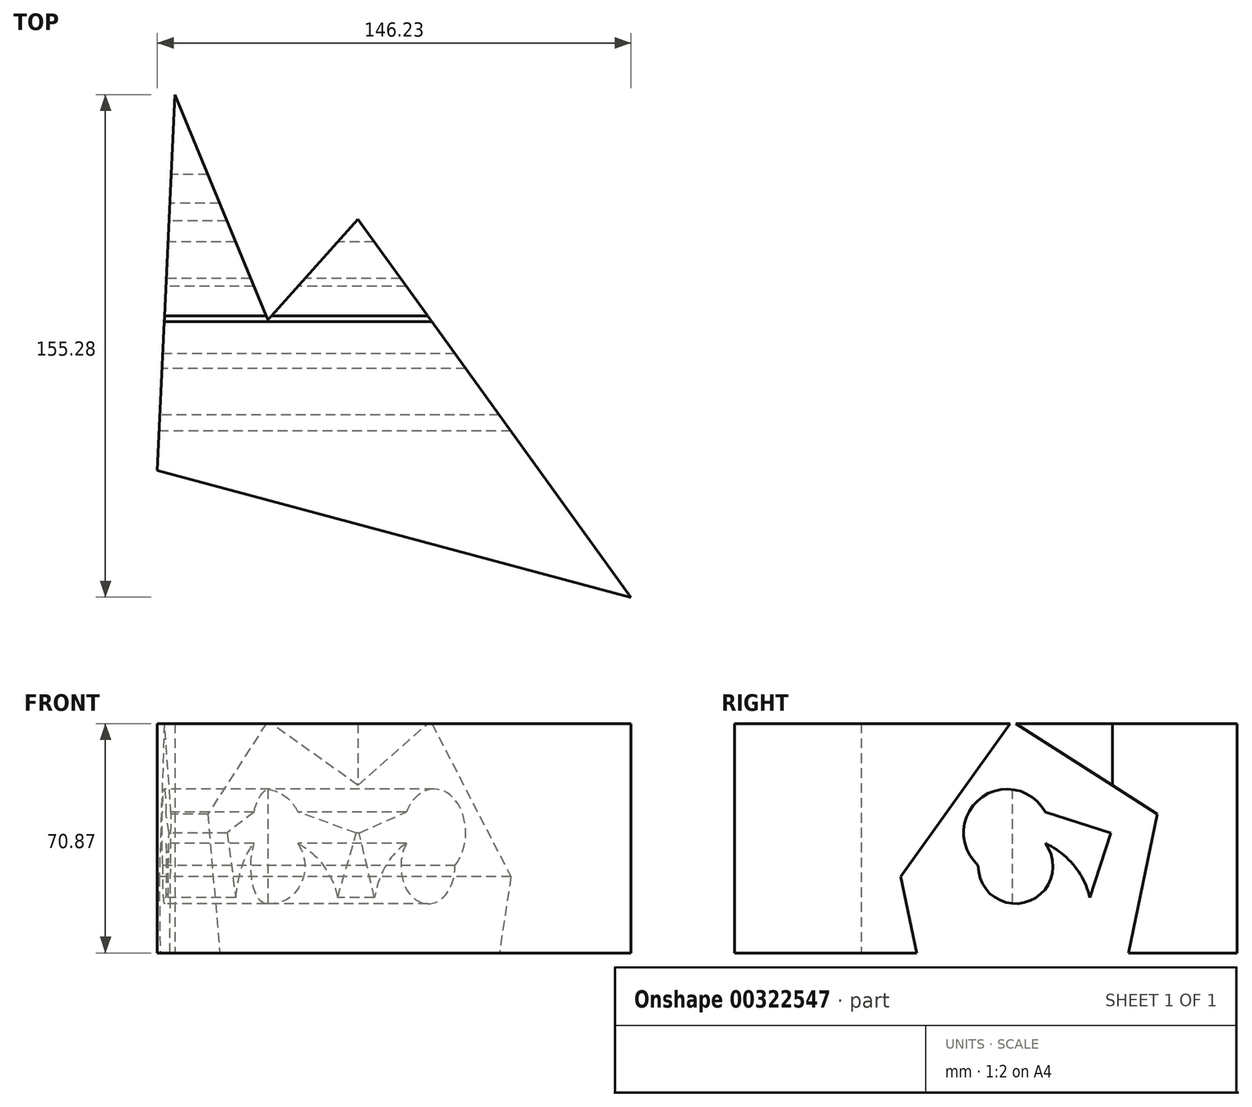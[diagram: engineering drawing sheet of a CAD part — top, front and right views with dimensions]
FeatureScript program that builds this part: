
annotation { "Feature Type Name" : "Feature", "Feature Type Description" : "" }
export const myFeature = defineFeature(function(context is Context, id is Id, definition is map)
    precondition{}
    {
        {
            var Q0;
            Q0=qCreatedBy(makeId("Top.planeOp"),FACE);
            var sketch = newSketch(context, id + "F0", { "sketchPlane" : qUnion([Q0])});
            skLineSegment(sketch, "E0", {"start": v(41.06, -46.52) * mm, "end": v(46.45, 69.58) * mm});
            skLineSegment(sketch, "E1", {"start": v(46.45, 69.58) * mm, "end": v(75.2, 0) * mm});
            skLineSegment(sketch, "E2", {"start": v(75.2, 0) * mm, "end": v(103.01, 31.07) * mm});
            skLineSegment(sketch, "E3", {"start": v(187.29, -85.7) * mm, "end": v(103.01, 31.07) * mm});
            skLineSegment(sketch, "E4", {"start": v(187.29, -85.7) * mm, "end": v(41.06, -46.52) * mm});
            skSolve(sketch);
        }
        {
            var Q0;
            Q0 = qSketchRegion(id + "F0", true);
            extrude(context, id + "F1", {"entities" : qUnion([Q0]), "depth" : 70.87 * mm});
        }
        {
            var Q0;
            Q0=qCreatedBy(makeId("Right.planeOp"),FACE);
            var sketch = newSketch(context, id + "F2", { "sketchPlane" : qUnion([Q0])});
            skLineSegment(sketch, "E5", {"start": v(36, 0) * mm, "end": v(44.9, 42.9) * mm});
            skLineSegment(sketch, "E6", {"start": v(44.9, 42.9) * mm, "end": v(0, 71.64) * mm});
            skLineSegment(sketch, "E7", {"start": v(0, 71.64) * mm, "end": v(-34.38, 23.58) * mm});
            skLineSegment(sketch, "E8", {"start": v(-34.38, 23.58) * mm, "end": v(-27.93, -6.78) * mm});
            skLineSegment(sketch, "E9", {"start": v(-27.93, -6.78) * mm, "end": v(36, 0) * mm});
            skLineSegment(sketch, "E10", {"start": v(24.06, 17.1) * mm, "end": v(30.5, 37.05) * mm});
            skLineSegment(sketch, "E11", {"start": v(30.5, 37.05) * mm, "end": v(10.35, 43.56) * mm});
            skArc(sketch, "E12", {"start": v(10.35, 43.56) * mm, "mid": v(-9.93, 47.71) * mm, "end": v(-10.48, 27.02) * mm});
            skArc(sketch, "E13", {"start": v(-10.48, 27.02) * mm, "mid": v(4.72, 15.74) * mm, "end": v(10.35, 33.8) * mm});
            skArc(sketch, "E14", {"start": v(24.06, 17.1) * mm, "mid": v(19.12, 27.02) * mm, "end": v(10.35, 33.8) * mm});
            skSolve(sketch);
        }
        {
            var Q0;
            Q0 = qSketchRegion(id + "F2", true);
            extrude(context, id + "F3", {"entities" : qUnion([Q0]), "operationType" : NewBodyOperationType.REMOVE, "depth" : 215.4 * mm});
        }
    });
